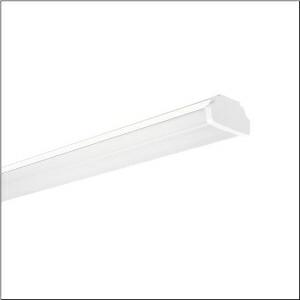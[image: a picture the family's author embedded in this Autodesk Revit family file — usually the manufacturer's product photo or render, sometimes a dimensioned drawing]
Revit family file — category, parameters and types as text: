
# Revit family: modario_r__31_gen_2_53bm8127v485c2_f877
name_source: partatom
category: Lighting Fixtures
units: mm (PartAtom-declared; Revit-internal decimal feet)

## family parameters
Cut with Voids When Loaded = No
Host = Face
Light Source = No
Part Type = Normal
Room Calculation Point = No
Round Connector Dimension = Use Diameter
Shared = No

## types (1)
- Modario® 31 Gen.2 (1 x LED, 8590 lm, 47.9 W, 4000K)
    Apparent Load = 48 VA
    CIE Flux Codes = 47 80 95 93 100
    Color Rendering = 80
    Color Temperature = 4000K
    Default Elevation = 1800 mm
    Description = Modario® 31 Gen.2, luminaire insert, of sheet steel, coil coated, white, length: 1.495mm, width: 81mm, height: 82mm, 5x system unit, system units: 299mm, LED rated luminous flux: 8.590lm, light colour: 840, control gear: ON/OFF, control gear: ECG, with plug, 3-pole, with phase selection, mains connection: 220..240V, AC, 50/60Hz, rated input power: 48W, through-wiring accessed according to module size, primary optical cover: cover, of PMMA, light emission: direct distribution, primary light characteristic: symmetric, protection rating (complete): IP20, protection rating (LED compartment): IP50, insulation class (complete): insulation class I (protective earthing), certification: CE, ENEC, VDE, UKCA, impact resistance: IK03, permissible ambient temperature for indoor applications: -35..+45°C, corresponds to IFS (International Featured Standards) requirements for safety and quality in the food industry, reducing of maximum allowable ambient temperature of 5°C with ceiling mounting, IP40 when using the optional accessory 5TP9018, packaging unit: 1 piece
    Height = 92 mm
    Lamp = 1 x LED
    Lamp Light Flux = 8590 lm
    Lamp Power = 47.9 W
    Lamp count = 1
    Length = 1495 mm
    Luminous efficacy = 179 lm/W
    Manufacturer = Siteco
    ModVariant = No
    Model = 53BM8127V485C2
    Mounting Place = Ceiling
    Mounting Type = Pendant
    Number of Poles = 1
    OnlyDefault = Yes
    Power Factor = 1
    Product Name = Modario® 31 Gen.2
    Product group = luminaire insert
    ProductGroupID = 902
    Protection Class = Protection class I
    Protection Degree = IP 20
    RLX_Detail_Level = 1
    RLX_Emergency_Light_Flux = 0 lm
    RLX_Emergency_Type = 0
    RLX_Emergency_Type_DB = No
    RlxData = <blob elided: 38741 chars, md5=cf9a57bc>
    Socket = socket
    Standby Power = 0 W
    System Light Flux = 8590 lm
    System Power = 48 W
    Type Comments = Product without accessories
    Type Image = l_1341886.jpg
    URL = http://relux.com
    VarID = ---
    Voltage = 0 V
    Weight = 0.00 kg
    Width = 81 mm

## geometry (parser evidence)
native form markers: Blend x4, Sweep x11
no freeform markers — native parametric forms only
